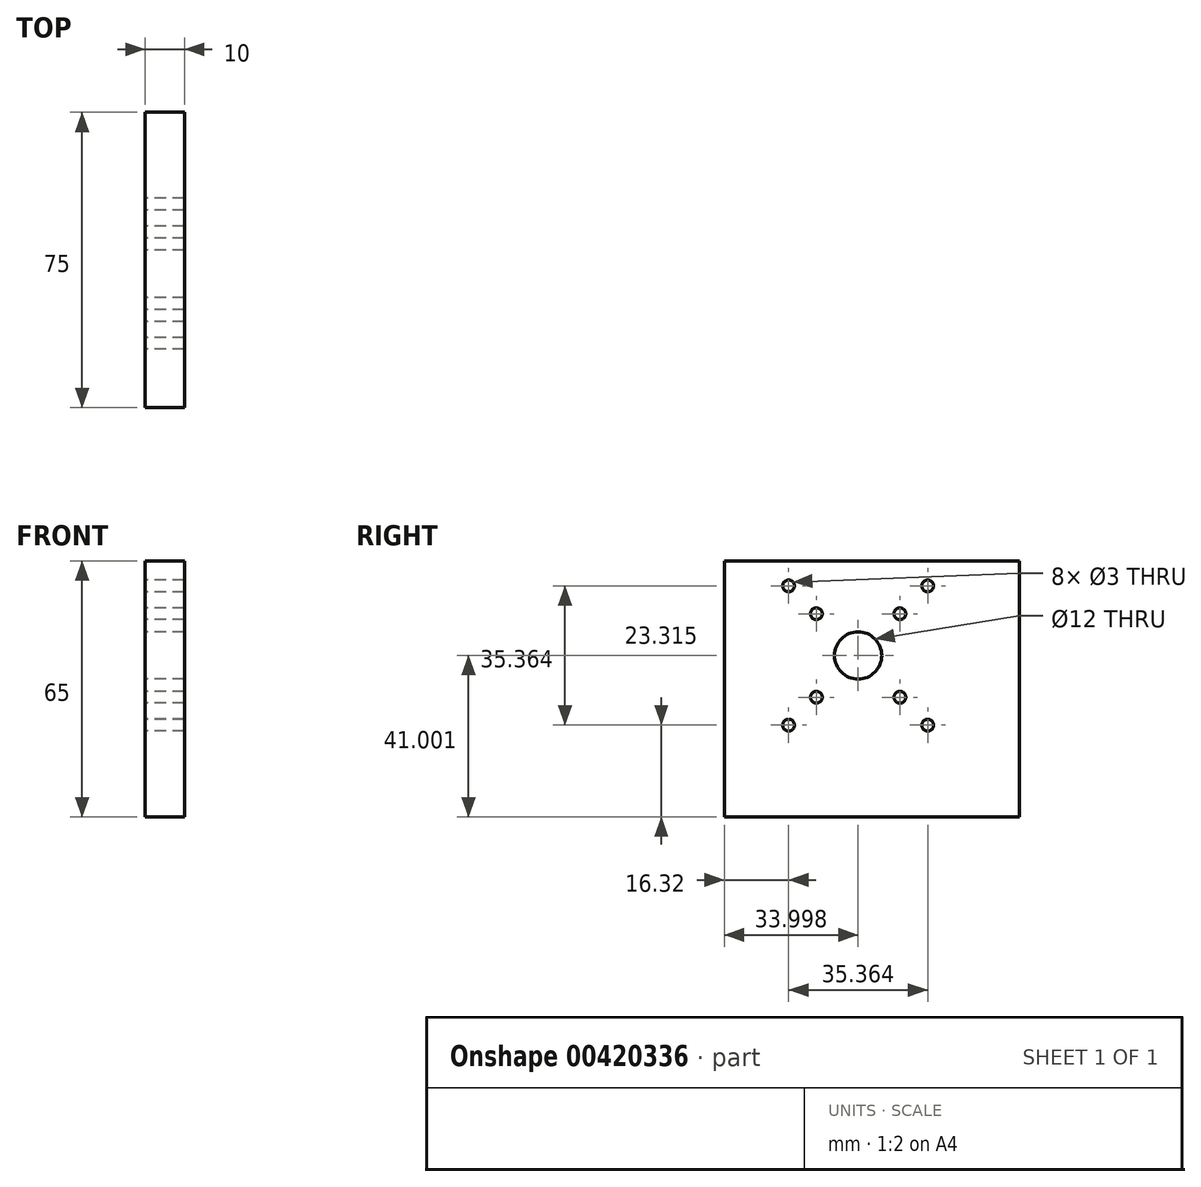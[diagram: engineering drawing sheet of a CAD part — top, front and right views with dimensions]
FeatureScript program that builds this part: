
annotation { "Feature Type Name" : "Feature", "Feature Type Description" : "" }
export const myFeature = defineFeature(function(context is Context, id is Id, definition is map)
    precondition{}
    {
        {
            var Q0;
            Q0=qCreatedBy(makeId("Right.planeOp"),FACE);
            var sketch = newSketch(context, id + "F0", { "sketchPlane" : qUnion([Q0])});
            skLineSegment(sketch, "E0.bottom", {"start": v(26.1, 39.64) * mm, "end": v(-48.9, 39.64) * mm});
            skLineSegment(sketch, "E0.top", {"start": v(26.1, -25.36) * mm, "end": v(-48.9, -25.36) * mm});
            skLineSegment(sketch, "E0.left", {"start": v(26.1, 39.64) * mm, "end": v(26.1, -25.36) * mm});
            skLineSegment(sketch, "E0.right", {"start": v(-48.9, 39.64) * mm, "end": v(-48.9, -25.36) * mm});
            skSolve(sketch);
        }
        {
            var Q0;
            Q0=qSketchRegion(id+"F0",true);
            extrude(context, id + "F1", {"entities" : qUnion([Q0]), "depth" : 10 * mm});
        }
        {
            var Q0;
            Q0=makeQuery(id+"F1.opExtrude","CAP_FACE",FACE,{"disambiguationData":[OSD([sQuery(id+"F0.wireOp",EDGE,"E0.bottom"),sQuery(id+"F0.wireOp",EDGE,"E0.top"),sQuery(id+"F0.wireOp",EDGE,"E0.left"),sQuery(id+"F0.wireOp",EDGE,"E0.right")])],"isStart":true});
            var sketch = newSketch(context, id + "F2", { "sketchPlane" : qUnion([Q0])});
            skCircle(sketch, "E1", {"center": v(14.9, 15.64) * mm, "radius": 6 * mm});
            skSolve(sketch);
        }
        {
            var Q0;
            Q0=qSketchRegion(id+"F2",true);
            extrude(context, id + "F3", {"entities" : qUnion([Q0]), "operationType" : NewBodyOperationType.REMOVE, "endBound" : BoundingType.THROUGH_ALL, "oppositeDirection" : true, "depth" : 25 * mm});
        }
        {
            var Q0;
            Q0=makeQuery(id+"F1.opExtrude","CAP_FACE",FACE,{"disambiguationData":[OSD([sQuery(id+"F0.wireOp",EDGE,"E0.bottom"),sQuery(id+"F0.wireOp",EDGE,"E0.top"),sQuery(id+"F0.wireOp",EDGE,"E0.left"),sQuery(id+"F0.wireOp",EDGE,"E0.right")])],"isStart":true});
            var sketch = newSketch(context, id + "F4", { "sketchPlane" : qUnion([Q0])});
            skLineSegment(sketch, "E2", {"start": v(-11.6, 42.13) * mm, "end": v(44.9, -14.37) * mm, "construction": true});
            skLineSegment(sketch, "E3", {"start": v(14.9, 15.64) * mm, "end": v(38.65, 39.39) * mm, "construction": true});
            skLineSegment(sketch, "E4", {"start": v(14.9, 15.64) * mm, "end": v(-5.01, -4.27) * mm, "construction": true});
            skCircle(sketch, "E5", {"center": v(4.3, 26.24) * mm, "radius": 1.5 * mm});
            skCircle(sketch, "E6", {"center": v(-2.78, 33.31) * mm, "radius": 1.5 * mm});
            skCircle(sketch, "E7.0.MirrorC", {"center": v(25.5, 5.03) * mm, "radius": 1.5 * mm});
            skCircle(sketch, "E7.1.MirrorC", {"center": v(32.58, -2.04) * mm, "radius": 1.5 * mm});
            skCircle(sketch, "E8", {"center": v(25.5, 26.25) * mm, "radius": 1.5 * mm});
            skCircle(sketch, "E9", {"center": v(32.58, 33.32) * mm, "radius": 1.5 * mm});
            skCircle(sketch, "E10.0.MirrorC", {"center": v(4.29, 5.03) * mm, "radius": 1.5 * mm});
            skCircle(sketch, "E10.1.MirrorC", {"center": v(-2.78, -2.05) * mm, "radius": 1.5 * mm});
            skSolve(sketch);
        }
        {
            var Q0;
            Q0=qSketchRegion(id+"F4",true);
            extrude(context, id + "F5", {"entities" : qUnion([Q0]), "operationType" : NewBodyOperationType.REMOVE, "endBound" : BoundingType.THROUGH_ALL, "oppositeDirection" : true, "depth" : 25 * mm});
        }
    });
